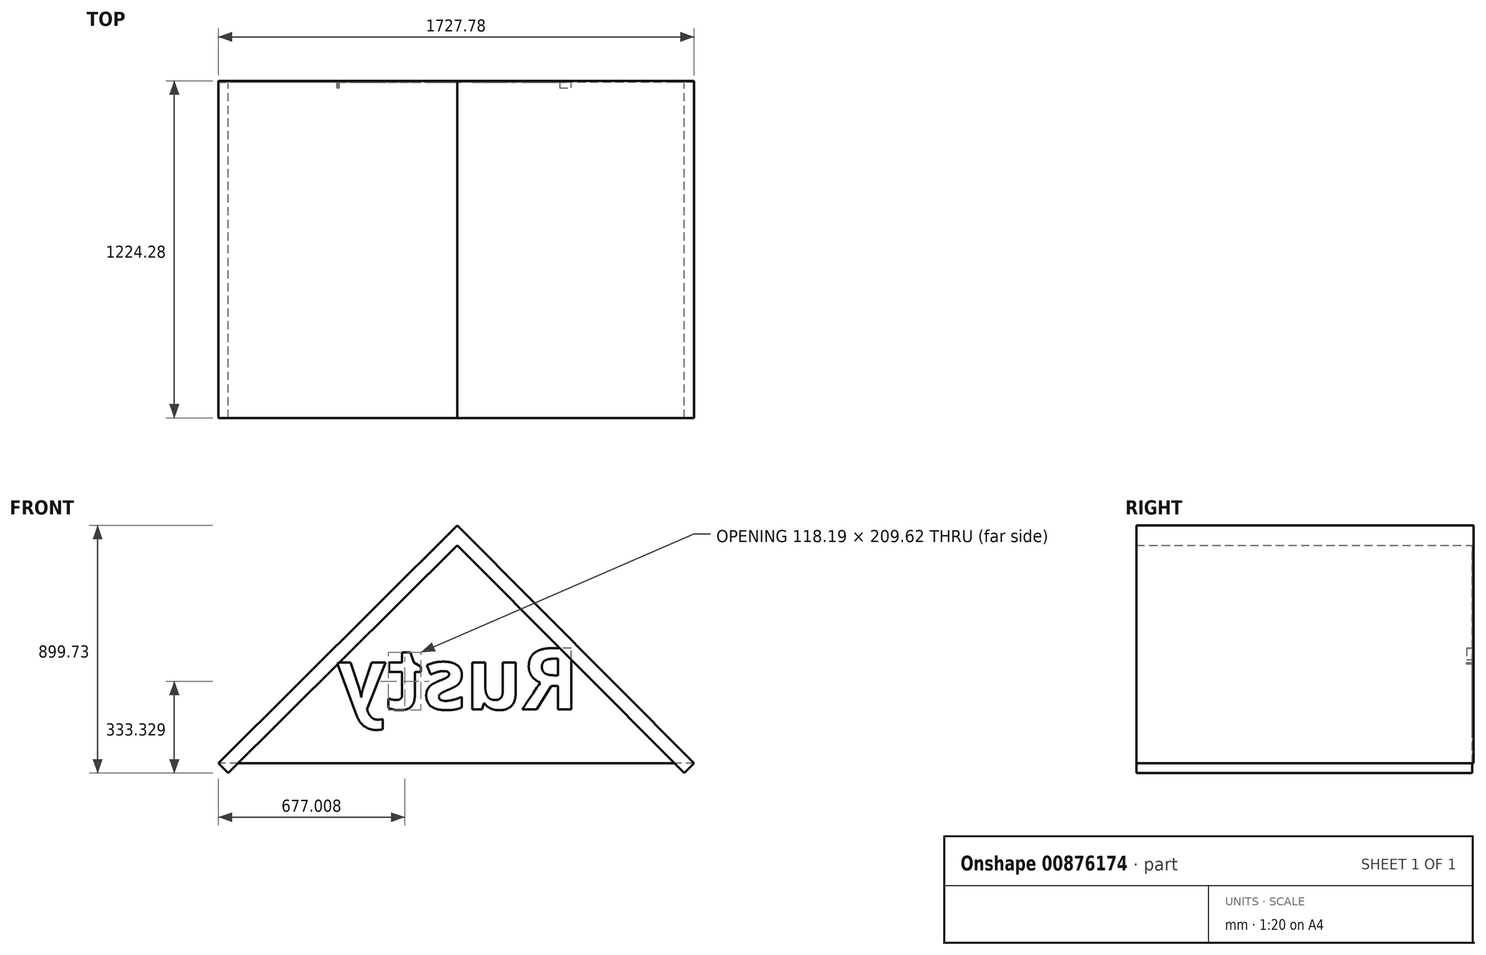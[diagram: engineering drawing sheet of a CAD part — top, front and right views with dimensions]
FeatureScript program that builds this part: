
annotation { "Feature Type Name" : "Feature", "Feature Type Description" : "" }
export const myFeature = defineFeature(function(context is Context, id is Id, definition is map)
    precondition{}
    {
        {
            var Q0;
            Q0=qCreatedBy(makeId("Front.planeOp"),FACE);
            var sketch = newSketch(context, id + "F0", { "sketchPlane" : qUnion([Q0])});
            skLineSegment(sketch, "E0", {"start": v(0, 863.88) * mm, "end": v(860.32, 0) * mm});
            skLineSegment(sketch, "E1", {"start": v(0, 863.88) * mm, "end": v(-867.46, 0) * mm});
            skLineSegment(sketch, "E2", {"start": v(860.32, 0) * mm, "end": v(824.33, -35.85) * mm});
            skLineSegment(sketch, "E3", {"start": v(824.33, -35.85) * mm, "end": v(0, 791.9) * mm});
            skLineSegment(sketch, "E4", {"start": v(0, 791.9) * mm, "end": v(-831.16, -35.85) * mm});
            skLineSegment(sketch, "E5", {"start": v(-867.46, 0) * mm, "end": v(-831.16, -35.85) * mm});
            skSolve(sketch);
        }
        {
            var Q0;
            Q0=makeQuery(id+"F0.imprint","IMPRINT",FACE,{"disambiguationData":[TD([[makeQuery(id+"F0.imprint","IMPRINT",EDGE,{"derivedFrom":sQuery(id+"F0.wireOp",EDGE,"E0")}),-1.0]])]});
            extrude(context, id + "F1", {"entities" : qUnion([Q0]), "depth" : 1219.2 * mm, "offsetDistance" : 25.4 * mm});
        }
        {
            var Q0;
            Q0=makeQuery(id+"F1.opExtrude","CAP_FACE",FACE,{"disambiguationData":[OSD([sQuery(id+"F0.wireOp",EDGE,"E0"),sQuery(id+"F0.wireOp",EDGE,"E1"),sQuery(id+"F0.wireOp",EDGE,"E2"),sQuery(id+"F0.wireOp",EDGE,"E3"),sQuery(id+"F0.wireOp",EDGE,"E4"),sQuery(id+"F0.wireOp",EDGE,"E5")])],"isStart":true});
            var sketch = newSketch(context, id + "F2", { "sketchPlane" : qUnion([Q0])});
            skLineSegment(sketch, "E6", {"start": v(0, 863.88) * mm, "end": v(-860.32, 0) * mm});
            skLineSegment(sketch, "E7", {"start": v(867.46, 0) * mm, "end": v(0, 863.88) * mm});
            skLineSegment(sketch, "E8", {"start": v(-860.32, 0) * mm, "end": v(867.46, 0) * mm});
            skSolve(sketch);
        }
        {
            var Q0;
            Q0=qSketchRegion(id+"F2",true);
            extrude(context, id + "F3", {"entities" : qUnion([Q0]), "operationType" : NewBodyOperationType.ADD, "depth" : 5.08 * mm, "offsetDistance" : 25.4 * mm});
        }
        {
            var Q0;
            Q0=makeQuery(id+"F3.opExtrude","CAP_FACE",FACE,{"disambiguationData":[OSD([sQuery(id+"F2.wireOp",EDGE,"E6"),sQuery(id+"F2.wireOp",EDGE,"E7"),sQuery(id+"F2.wireOp",EDGE,"E8")])],"isStart":false});
            var sketch = newSketch(context, id + "F4", { "sketchPlane" : qUnion([Q0])});
            skText(sketch, "E9", { "text": "Rusty", "fontName": "OpenSans-Bold.ttf"});
            const initialGuessF4  = {"E9": [-0.44174, 0.19574, 1, 0, 0.22458]};
            skSetInitialGuess(sketch, initialGuessF4);
            skSolve(sketch);
        }
        {
            var Q0;
            Q0=qSketchRegion(id+"F4",true);
            extrude(context, id + "F5", {"entities" : qUnion([Q0]), "operationType" : NewBodyOperationType.REMOVE, "oppositeDirection" : true, "depth" : 25.4 * mm, "offsetDistance" : 25.4 * mm});
        }
    });
